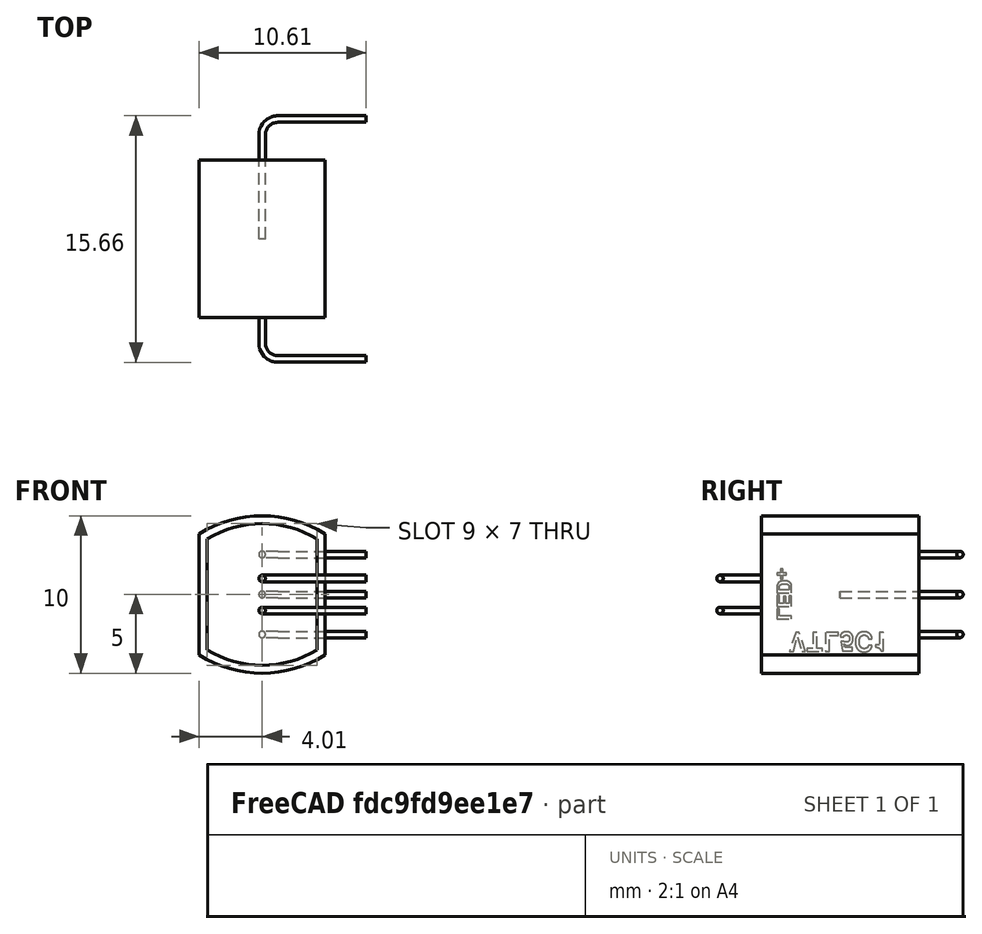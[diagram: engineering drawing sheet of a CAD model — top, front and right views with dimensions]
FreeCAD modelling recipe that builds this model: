
FCSTD DOCUMENT  (FreeCAD 0.19R16945 (Git))
Label: Vactec_VTL5C1
License: All rights reserved
LicenseURL: http://en.wikipedia.org/wiki/All_rights_reserved
objects: PartDesign::Body×7, PartDesign::FeatureBase×5, Sketcher::SketchObject×4, Part::Part2DObjectPython×2, Part::Extrusion×2, PartDesign::Pad×1, PartDesign::Pocket×1, PartDesign::Mirrored×1, PartDesign::AdditivePipe×1, Spreadsheet::Sheet×1, Part::MultiFuse×1
note: 28 computed .brp shape members not serialized (recipe doc carries the construction recipe); baked Part::Feature solids carry a one-line shape summary decoded from their .brp

FEATURE [Sketcher::SketchObject] Sketch
  MapMode = 5
  Placement = pos=(0,0,0) rot=(1,0,0;1.5708rad)
  Support = -> [XZ_Plane]
  expr: Constraints[12] = Spreadsheet.bodyheight
  expr: Constraints[13] = Spreadsheet.bodylength
  sketch-geometry (6):
    g0: LineSegment StartX=-4 StartY=3.84429 StartZ=0 EndX=-4 EndY=-3.84429 EndZ=0
    g1: LineSegment StartX=4 StartY=3.84429 StartZ=0 EndX=4 EndY=-3.84429 EndZ=0
    g2: ArcOfCircle CenterX=0 CenterY=-2.5 CenterZ=0 NormalX=0 NormalY=0 NormalZ=1 AngleXU=0 Radius=7.5 StartAngle=1.00826 EndAngle=2.13333
    g3: ArcOfCircle CenterX=0 CenterY=2.5 CenterZ=0 NormalX=0 NormalY=0 NormalZ=1 AngleXU=0 Radius=7.5 StartAngle=4.14985 EndAngle=5.27493
    g4: GeomPoint X=0 Y=5 Z=0
    g5: GeomPoint X=0 Y=-5 Z=0
  constraints (16):
    c: Vertical(g1)
    c: PointOnObject(g2,g-2)
    c: Coincident(g2,g0)
    c: Coincident(g2,g1)
    c: PointOnObject(g3,g-2)
    c: Coincident(g3,g0)
    c: Coincident(g3,g1)
    c: PointOnObject(g4,g2)
    c: PointOnObject(g5,g3)
    c: PointOnObject(g4,g-2)
    c: Symmetric(g0,g0,g-1)
    c: Equal(g2,g3)
    c: DistanceX(g0,g1) = 8
    c: DistanceY(g5,g4) = 10
    c: Equal(g1,g0)
    c: Symmetric(g5,g-1,g2)
FEATURE [PartDesign::Pad] Pad
  Length = 10
  Length2 = 100
  Midplane = true
  Placement = pos=(0,0,0) rot=(1,0,0;1.5708rad)
  Profile = -> Sketch
  Type = 0
FEATURE [Sketcher::SketchObject] Sketch001
  MapMode = 5
  Placement = pos=(0,-5,-1.1e-15) rot=(1,0,0;1.5708rad)
  Support = -> [Pad]
  expr: Constraints[13] = Sketch.Constraints[13] - 1mm
  expr: Constraints[12] = Sketch.Constraints[12] - 1mm
  sketch-geometry (6):
    g0: LineSegment StartX=-3.5 StartY=3.5217 StartZ=0 EndX=-3.5 EndY=-3.5217 EndZ=0
    g1: LineSegment StartX=3.5 StartY=3.5217 StartZ=0 EndX=3.5 EndY=-3.5217 EndZ=0
    g2: ArcOfCircle CenterX=0 CenterY=-2.25 CenterZ=0 NormalX=0 NormalY=0 NormalZ=1 AngleXU=0 Radius=6.75 StartAngle=1.02568 EndAngle=2.11591
    g3: ArcOfCircle CenterX=0 CenterY=2.25 CenterZ=0 NormalX=0 NormalY=0 NormalZ=1 AngleXU=0 Radius=6.75 StartAngle=4.16727 EndAngle=5.25751
    g4: GeomPoint X=0 Y=4.5 Z=0
    g5: GeomPoint X=0 Y=-4.5 Z=0
  constraints (16):
    c: Vertical(g1)
    c: PointOnObject(g2,g-2)
    c: Coincident(g2,g0)
    c: Coincident(g2,g1)
    c: PointOnObject(g3,g-2)
    c: Coincident(g3,g0)
    c: Coincident(g3,g1)
    c: PointOnObject(g4,g2)
    c: PointOnObject(g5,g3)
    c: PointOnObject(g4,g-2)
    c: Symmetric(g0,g0,g-1)
    c: Equal(g2,g3)
    c: DistanceX(g0,g1) = 7
    c: DistanceY(g5,g4) = 9
    c: Equal(g1,g0)
    c: Symmetric(g5,g-1,g2)
FEATURE [PartDesign::Pocket] Pocket
  BaseFeature = -> Pad
  Length = 0.01
  Length2 = 100
  Placement = pos=(0,0,0) rot=(1,0,0;1.5708rad)
  Profile = -> Sketch001
  Type = 0
FEATURE [PartDesign::Mirrored] Mirrored
  BaseFeature = -> Pocket
  MirrorPlane = -> XZ_Plane
  Originals = -> [Pocket]
  Placement = pos=(0,0,0) rot=(1,0,0;1.5708rad)
FEATURE [PartDesign::Body] Body
  Group = -> [Sketch,Pad,Sketch001,Pocket,Mirrored]
  Origin = -> Origin
  Tip = -> Mirrored
FEATURE [Sketcher::SketchObject] Sketch004  label="LeadDiameter"
  AttachmentOffset = pos=(0,0,4) rot=(0,0,1;0rad)
  MapMode = 5
  Placement = pos=(0,-4,-9e-16) rot=(1,0,0;1.5708rad)
  Support = -> [XZ_Plane002]
  expr: AttachmentOffset.Base.z = Spreadsheet.bodylength / 2 - 1mm
  expr: AttachmentOffset.Base.y = 0
  expr: Constraints[1] = Spreadsheet.leaddialed / 2
  sketch-geometry (1):
    g0: Circle CenterX=0 CenterY=0 CenterZ=0 NormalX=0 NormalY=0 NormalZ=1 AngleXU=0 Radius=0.2075
  constraints (2):
    c: Coincident(g0,g-1)
    c: Radius(g0) = 0.2075
FEATURE [Sketcher::SketchObject] Sketch005  label="LeadProfile"
  MapMode = 5
  Support = -> [XY_Plane002]
  expr: Constraints[6] = Spreadsheet.leadpitch / 2
  expr: Constraints[7] = Spreadsheet.bodyheight / 2 + Spreadsheet.leadextralength
  sketch-geometry (3):
    g0: LineSegment StartX=0 StartY=0 StartZ=0 EndX=0 EndY=-6.62 EndZ=0
    g1: LineSegment StartX=1 StartY=-7.62 StartZ=0 EndX=6.6 EndY=-7.62 EndZ=0
    g2: ArcOfCircle CenterX=1 CenterY=-6.62 CenterZ=0 NormalX=0 NormalY=0 NormalZ=1 AngleXU=0 Radius=1 StartAngle=3.14159 EndAngle=4.71239
  constraints (8):
    c: Coincident(g0,g-1)
    c: Horizontal(g1)
    c: Tangent(g0,g2) = -1.5708
    c: Tangent(g1,g2) = -1.5708
    c: Radius(g2) = 1
    c: PointOnObject(g0,g-2)
    c: DistanceY(g1,g0) = 7.62
    c: DistanceX(g0,g1) = 6.6
FEATURE [PartDesign::AdditivePipe] AdditivePipe
  AuxilleryCurvelinear = true
  AuxillerySpineTangent = false
  Binormal = (0,0,0)
  Mode = 0
  Placement = pos=(0,0,0) rot=(1,0,0;1.5708rad)
  Profile = -> Sketch004
  Spine = -> Sketch005
  SpineTangent = false
  Transformation = 0
  Transition = 0
FEATURE [PartDesign::Body] Body002  label="Lead"
  Group = -> [Sketch004,Sketch005,AdditivePipe]
  Origin = -> Origin002
  Tip = -> AdditivePipe
FEATURE [Spreadsheet::Sheet] Spreadsheet
  cells = A2=bodylength; B2(bodylength)==10mm; A3=bodyheight; B3(bodyheight)==8mm; A4=pottingmaxheight; B4(pottingmaxheight)==2.5mm; A6=leaddialed; B6(leaddialed)==0.415mm; A7=leadpitchled; B7(leadpitchled)==2.035mm; A8=leadpitchldr; B8(leadpitchldr)==5.08mm; A10=leadpitch; B10(leadpitch)==6 * 2.54mm; A11=leadextralength; B11(leadextralength)==2.6mm
FEATURE [Part::Part2DObjectPython] ShapeString  # Draft 2D object (typed FeaturePython)
  AttachmentOffset = pos=(5.5,-1,0) rot=(0,0,1;3.14159rad)
  FontFile = <userpath>/Desktop/GitHub/freecad-projects/00-fonts/FreeSansBold.ttf
  MapMode = 6
  Placement = pos=(-4,-4,-1.65571) rot=(0,-1,0;1.5708rad)
  Size = 0.5
  String = LED+
  Support = -> [Mirrored]
  Tracking = 0
FEATURE [Part::Extrusion] Extrude  label="MarkingLED"
  Base = -> ShapeString
  Dir = (-1,0,-2e-16)
  DirMode = 2
  FaceMakerClass = Part::FaceMakerBullseye
  LengthFwd = 0.01
  LengthRev = 0
  Solid = false
  Symmetric = false
FEATURE [Part::Part2DObjectPython] ShapeString001  # Draft 2D object (typed FeaturePython)
  AttachmentOffset = pos=(6.25,-1.75,0) rot=(0,0,1;-1.5708rad)
  FontFile = <userpath>/Desktop/GitHub/freecad-projects/00-fonts/FreeSansBold.ttf
  MapMode = 6
  Placement = pos=(-4,-3.25,-2.40571) rot=(-0.57735,-0.57735,0.57735;2.0944rad)
  Size = 0.65
  String = VTL5C1
  Support = -> [Mirrored]
  Tracking = 0
FEATURE [Part::Extrusion] Extrude001  label="MarkingVTL"
  Base = -> ShapeString001
  Dir = (-1,0,-2e-16)
  DirMode = 2
  FaceMakerClass = Part::FaceMakerBullseye
  LengthFwd = 0.01
  LengthRev = 0
  Solid = false
  Symmetric = false
FEATURE [PartDesign::FeatureBase] Clone
  BaseFeature = -> Body002
FEATURE [PartDesign::Body] Body003  label="LeadCloneLED1"
  BaseFeature = -> Body002
  Group = -> [Clone]
  Origin = -> Origin003
  Placement = pos=(0,0,1.0175) rot=(0,0,1;0rad)
  Tip = -> Clone
  expr: Placement.Base.z = Spreadsheet.leadpitchled / 2
FEATURE [PartDesign::FeatureBase] Clone001
  BaseFeature = -> Body002
FEATURE [PartDesign::Body] Body004  label="LeadCloneLED2"
  BaseFeature = -> Body002
  Group = -> [Clone001]
  Origin = -> Origin004
  Placement = pos=(0,0,-1.0175) rot=(0,0,1;0rad)
  Tip = -> Clone001
  expr: Placement.Base.z = -Spreadsheet.leadpitchled / 2
FEATURE [PartDesign::FeatureBase] Clone002
  BaseFeature = -> Body002
FEATURE [PartDesign::Body] Body005  label="LeadCloneLDR1"
  BaseFeature = -> Body002
  Group = -> [Clone002]
  Origin = -> Origin005
  Placement = pos=(0,0,2.54) rot=(1,0,0;3.14159rad)
  Tip = -> Clone002
  expr: Placement.Base.z = Spreadsheet.leadpitchldr / 2
FEATURE [PartDesign::FeatureBase] Clone003
  BaseFeature = -> Body002
FEATURE [PartDesign::Body] Body006  label="LeadCloneLDR2"
  BaseFeature = -> Body002
  Group = -> [Clone003]
  Origin = -> Origin006
  Placement = pos=(0,0,-2.54) rot=(1,0,0;3.14159rad)
  Tip = -> Clone003
  expr: Placement.Base.z = -Spreadsheet.leadpitchldr / 2
FEATURE [PartDesign::FeatureBase] Clone004
  BaseFeature = -> Body002
FEATURE [PartDesign::Body] Body007  label="LeadCloneLDR3"
  BaseFeature = -> Body002
  Group = -> [Clone004]
  Origin = -> Origin007
  Placement = pos=(0,0,0) rot=(1,0,0;3.14159rad)
  Tip = -> Clone004
FEATURE [Part::MultiFuse] Fusion  label="Vactec_VTL5C1"
  Shapes = -> [Body006,Body003,Extrude,Extrude001,Body005,Body004,Body]
